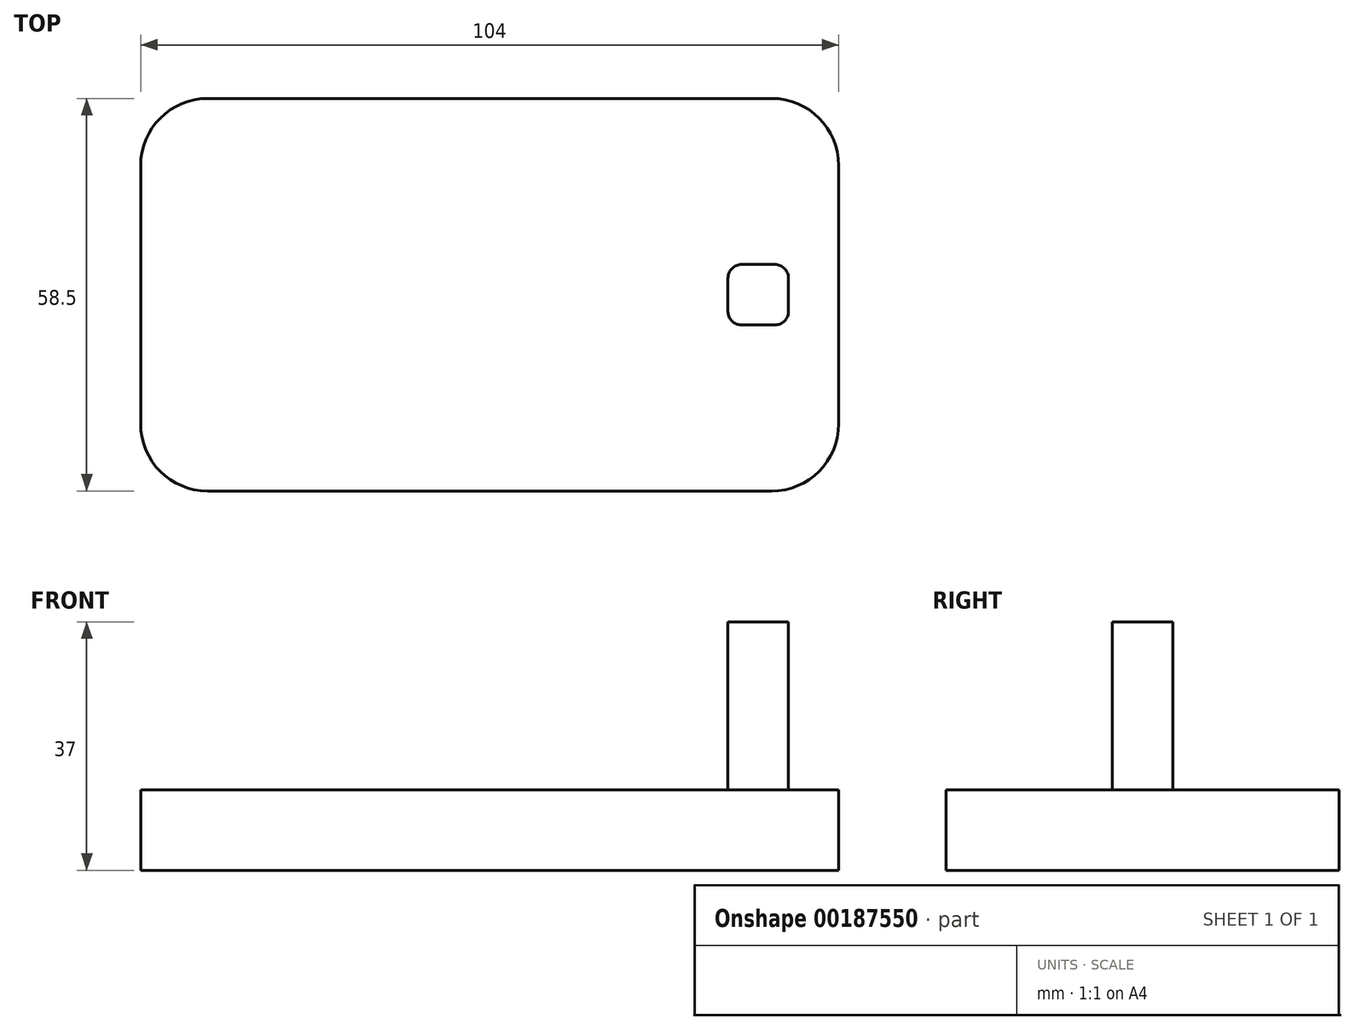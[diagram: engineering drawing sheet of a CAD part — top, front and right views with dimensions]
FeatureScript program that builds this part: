
annotation { "Feature Type Name" : "Feature", "Feature Type Description" : "" }
export const myFeature = defineFeature(function(context is Context, id is Id, definition is map)
    precondition{}
    {
        {
            var Q0;
            Q0=qCreatedBy(makeId("Top.planeOp"),FACE);
            var sketch = newSketch(context, id + "F0", { "sketchPlane" : qUnion([Q0])});
            skLineSegment(sketch, "E0.bottom", {"start": v(-42, 29.25) * mm, "end": v(42, 29.25) * mm});
            skLineSegment(sketch, "E0.top", {"start": v(-42, -29.25) * mm, "end": v(42, -29.25) * mm});
            skLineSegment(sketch, "E0.left", {"start": v(-52, 19.25) * mm, "end": v(-52, -19.25) * mm});
            skLineSegment(sketch, "E0.right", {"start": v(52, 19.25) * mm, "end": v(52, -19.25) * mm});
            skPoint(sketch, "E0.middle", {"position": v(0, 0) * mm});
            skPoint(sketch, "E1.visualSharp", {"position": v(-52, -29.25) * mm});
            skArc(sketch, "E1.filletArc", {"start": v(-52, -19.25) * mm, "mid": v(-49.07, -26.32) * mm, "end": v(-42, -29.25) * mm});
            skPoint(sketch, "E2.visualSharp", {"position": v(-52, 29.25) * mm});
            skArc(sketch, "E2.filletArc", {"start": v(-42, 29.25) * mm, "mid": v(-49.07, 26.32) * mm, "end": v(-52, 19.25) * mm});
            skPoint(sketch, "E3.visualSharp", {"position": v(52, 29.25) * mm});
            skArc(sketch, "E3.filletArc", {"start": v(52, 19.25) * mm, "mid": v(49.07, 26.32) * mm, "end": v(42, 29.25) * mm});
            skPoint(sketch, "E4.visualSharp", {"position": v(52, -29.25) * mm});
            skArc(sketch, "E4.filletArc", {"start": v(42, -29.25) * mm, "mid": v(49.07, -26.32) * mm, "end": v(52, -19.25) * mm});
            skSolve(sketch);
        }
        {
            var Q0;
            Q0=makeQuery(id+"F0.imprint","IMPRINT",FACE,{"disambiguationData":[TD([[makeQuery(id+"F0.imprint","IMPRINT",EDGE,{"derivedFrom":sQuery(id+"F0.wireOp",EDGE,"E0.bottom")}),-1.0]])]});
            var Q1;
            Q1=sQuery(id+"F0.wireOp",EDGE,"E0.top");
            var Q2;
            Q2=sQuery(id+"F0.wireOp",EDGE,"E0.left");
            var Q3;
            Q3=sQuery(id+"F0.wireOp",EDGE,"E0.right");
            var Q4;
            Q4=sQuery(id+"F0.wireOp",EDGE,"E0.bottom");
            extrude(context, id + "F1", {"entities" : qUnion([Q0]), "surfaceEntities" : qUnion([Q1, Q2, Q3, Q4]), "depth" : 12 * mm});
        }
        {
            var Q0;
            Q0=makeQuery(id+"F1.opExtrude","CAP_FACE",FACE,{"disambiguationData":[OSD([sQuery(id+"F0.wireOp",EDGE,"E0.bottom"),sQuery(id+"F0.wireOp",EDGE,"E0.top"),sQuery(id+"F0.wireOp",EDGE,"E0.left"),sQuery(id+"F0.wireOp",EDGE,"E0.right"),sQuery(id+"F0.wireOp",EDGE,"E1.filletArc"),sQuery(id+"F0.wireOp",EDGE,"E2.filletArc"),sQuery(id+"F0.wireOp",EDGE,"E3.filletArc"),sQuery(id+"F0.wireOp",EDGE,"E4.filletArc")])],"isStart":false});
            var sketch = newSketch(context, id + "F2", { "sketchPlane" : qUnion([Q0])});
            skLineSegment(sketch, "E5.bottom", {"start": v(37.5, 4.5) * mm, "end": v(42.5, 4.5) * mm});
            skLineSegment(sketch, "E5.top", {"start": v(37.5, -4.5) * mm, "end": v(42.5, -4.5) * mm});
            skLineSegment(sketch, "E5.left", {"start": v(35.5, 2.5) * mm, "end": v(35.5, -2.5) * mm});
            skLineSegment(sketch, "E5.right", {"start": v(44.5, 2.5) * mm, "end": v(44.5, -2.5) * mm});
            skPoint(sketch, "E5.middle", {"position": v(40, 0) * mm});
            skPoint(sketch, "E6.visualSharp", {"position": v(35.5, -4.5) * mm});
            skArc(sketch, "E6.filletArc", {"start": v(35.5, -2.5) * mm, "mid": v(36.09, -3.91) * mm, "end": v(37.5, -4.5) * mm});
            skPoint(sketch, "E7.visualSharp", {"position": v(35.5, 4.5) * mm});
            skArc(sketch, "E7.filletArc", {"start": v(37.5, 4.5) * mm, "mid": v(36.09, 3.91) * mm, "end": v(35.5, 2.5) * mm});
            skPoint(sketch, "E8.visualSharp", {"position": v(44.5, 4.5) * mm});
            skArc(sketch, "E8.filletArc", {"start": v(44.5, 2.5) * mm, "mid": v(43.91, 3.91) * mm, "end": v(42.5, 4.5) * mm});
            skPoint(sketch, "E9.visualSharp", {"position": v(44.5, -4.5) * mm});
            skArc(sketch, "E9.filletArc", {"start": v(42.5, -4.5) * mm, "mid": v(43.91, -3.91) * mm, "end": v(44.5, -2.5) * mm});
            skSolve(sketch);
        }
        {
            var Q0;
            Q0=makeQuery(id+"F2.imprint","IMPRINT",FACE,{"disambiguationData":[TD([[makeQuery(id+"F2.imprint","IMPRINT",EDGE,{"derivedFrom":sQuery(id+"F2.wireOp",EDGE,"E5.bottom")}),-1.0]])]});
            extrude(context, id + "F3", {"entities" : qUnion([Q0]), "operationType" : NewBodyOperationType.ADD, "depth" : 25 * mm});
        }
    });
